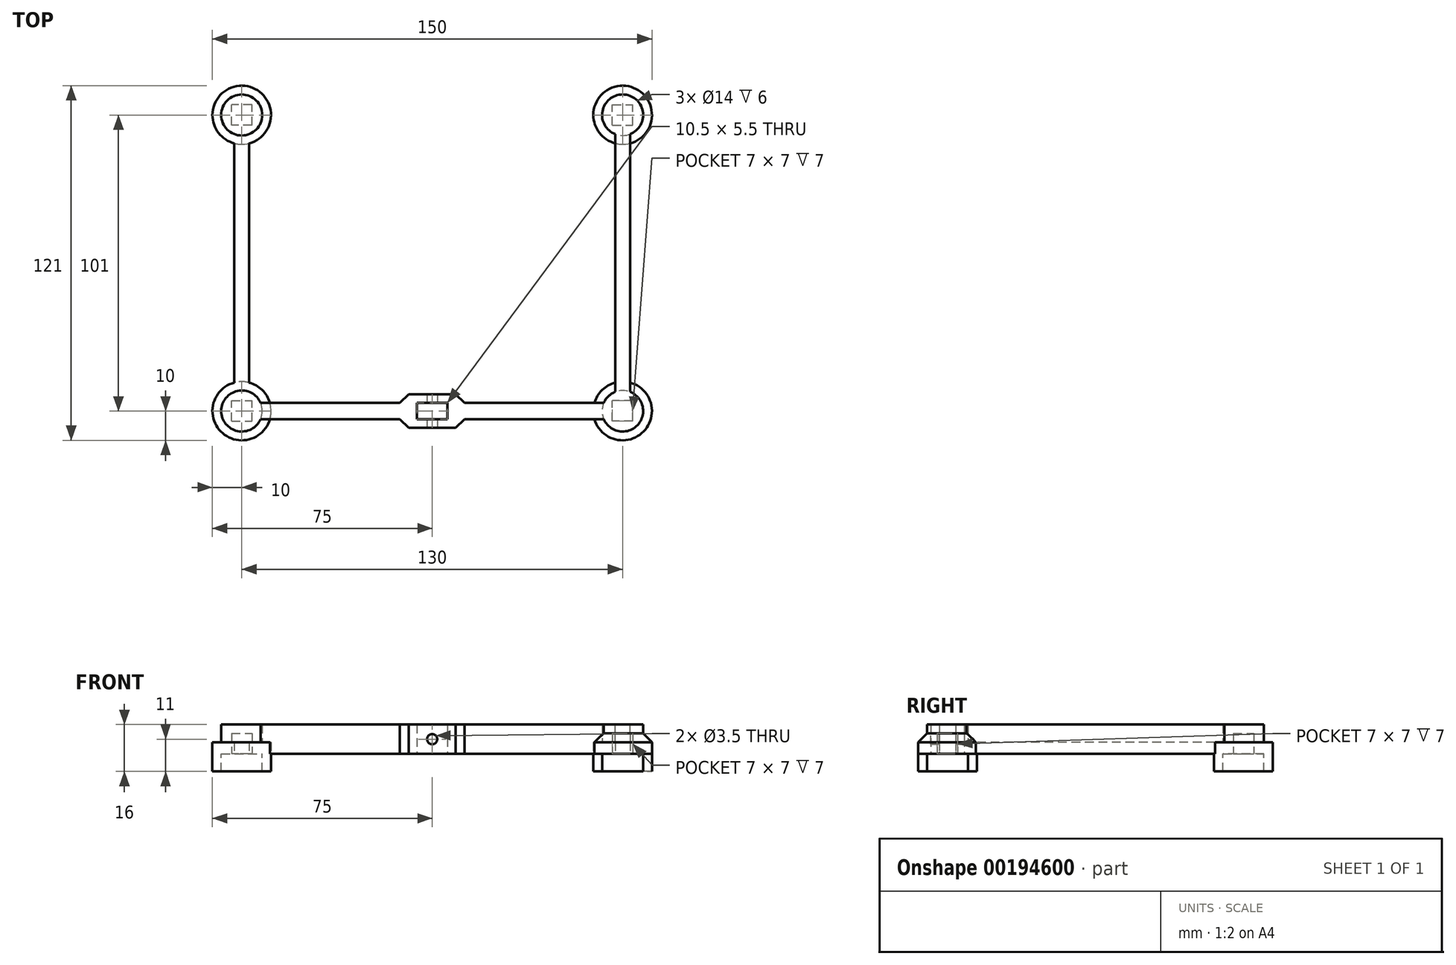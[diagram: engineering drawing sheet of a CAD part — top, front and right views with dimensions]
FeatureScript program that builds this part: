
annotation { "Feature Type Name" : "Feature", "Feature Type Description" : "" }
export const myFeature = defineFeature(function(context is Context, id is Id, definition is map)
    precondition{}
    {
        {
            var Q0;
            Q0=qCreatedBy(makeId("Top.planeOp"),FACE);
            var sketch = newSketch(context, id + "F0", { "sketchPlane" : qUnion([Q0])});
            skLineSegment(sketch, "E0.bottom", {"start": v(-5.25, 2.75) * mm, "end": v(5.25, 2.75) * mm});
            skLineSegment(sketch, "E0.top", {"start": v(-5.25, -2.75) * mm, "end": v(5.25, -2.75) * mm});
            skLineSegment(sketch, "E0.left", {"start": v(-5.25, 2.75) * mm, "end": v(-5.25, -2.75) * mm});
            skLineSegment(sketch, "E0.right", {"start": v(5.25, 2.75) * mm, "end": v(5.25, -2.75) * mm});
            skPoint(sketch, "E0.middle", {"position": v(0, 0) * mm});
            skLineSegment(sketch, "E1.bottom", {"start": v(-8, 5.75) * mm, "end": v(8, 5.75) * mm});
            skLineSegment(sketch, "E1.top", {"start": v(-8, -5.75) * mm, "end": v(8, -5.75) * mm});
            skLineSegment(sketch, "E1.left", {"start": v(-8, 5.75) * mm, "end": v(-8, -5.75) * mm});
            skLineSegment(sketch, "E1.right", {"start": v(8, 5.75) * mm, "end": v(8, -5.75) * mm});
            skLineSegment(sketch, "E2", {"start": v(0, 0) * mm, "end": v(-65, 0) * mm, "construction": true});
            skCircle(sketch, "E3", {"center": v(-65, 0) * mm, "radius": 7 * mm});
            skCircle(sketch, "E4", {"center": v(-65, 0) * mm, "radius": 10 * mm});
            skLineSegment(sketch, "E5", {"start": v(-8, 2.75) * mm, "end": v(-55.39, 2.75) * mm});
            skLineSegment(sketch, "E6", {"start": v(-8, -2.75) * mm, "end": v(-55.39, -2.75) * mm});
            skLineSegment(sketch, "E7.MirrorCS", {"start": v(8, -2.75) * mm, "end": v(55.39, -2.75) * mm});
            skLineSegment(sketch, "E8.MirrorCS", {"start": v(8, 2.75) * mm, "end": v(55.39, 2.75) * mm});
            skCircle(sketch, "E9.MirrorC", {"center": v(65, 0) * mm, "radius": 7 * mm});
            skCircle(sketch, "E10.MirrorC", {"center": v(65, 0) * mm, "radius": 10 * mm});
            skSolve(sketch);
        }
        {
            var Q0;
            Q0=makeQuery(id+"F0.imprint","IMPRINT",FACE,{"disambiguationData":[TD([[makeQuery(id+"F0.imprint","IMPRINT",EDGE,{"derivedFrom":sQuery(id+"F0.wireOp",EDGE,"E3")}),-1.0]])]});
            var Q1;
            Q1=makeQuery(id+"F0.imprint","IMPRINT",FACE,{"disambiguationData":[TD([[makeQuery(id+"F0.imprint","IMPRINT",EDGE,{"derivedFrom":sQuery(id+"F0.wireOp",EDGE,"E9.MirrorC")}),1.0]])]});
            extrude(context, id + "F1", {"entities" : qUnion([Q0, Q1]), "oppositeDirection" : true, "depth" : 6 * mm});
        }
        {
            var Q0;
            {var subQ0=sQuery(id+"F0.wireOp",EDGE,"E5");Q0=makeQuery(id+"F0.imprint","IMPRINT",FACE,{"disambiguationData":[TD([[makeQuery(id+"F0.imprint","IMPRINT",EDGE,{"derivedFrom":subQ0}),1.0]])]});}
            var Q1;
            {var subQ0=sQuery(id+"F0.wireOp",EDGE,"E7.MirrorCS");Q1=makeQuery(id+"F0.imprint","IMPRINT",FACE,{"disambiguationData":[TD([[makeQuery(id+"F0.imprint","IMPRINT",EDGE,{"derivedFrom":subQ0}),1.0]])]});}
            var Q2;
            Q2=makeQuery(id+"F0.imprint","IMPRINT",FACE,{"disambiguationData":[TD([[makeQuery(id+"F0.imprint","IMPRINT",EDGE,{"derivedFrom":sQuery(id+"F0.wireOp",EDGE,"E9.MirrorC")}),1.0]])]});
            var Q3;
            Q3=makeQuery(id+"F0.imprint","IMPRINT",FACE,{"disambiguationData":[TD([[makeQuery(id+"F0.imprint","IMPRINT",EDGE,{"derivedFrom":sQuery(id+"F0.wireOp",EDGE,"E0.bottom")}),1.0]])]});
            var Q4;
            Q4=makeQuery(id+"F0.imprint","IMPRINT",FACE,{"disambiguationData":[TD([[makeQuery(id+"F0.imprint","IMPRINT",EDGE,{"derivedFrom":sQuery(id+"F0.wireOp",EDGE,"E3")}),1.0]])]});
            var Q5;
            Q5=makeQuery(id+"F0.imprint","IMPRINT",FACE,{"disambiguationData":[TD([[makeQuery(id+"F0.imprint","IMPRINT",EDGE,{"derivedFrom":sQuery(id+"F0.wireOp",EDGE,"E3")}),-1.0]])]});
            var Q6;
            Q6=makeQuery(id+"F0.imprint","IMPRINT",FACE,{"disambiguationData":[TD([[makeQuery(id+"F0.imprint","IMPRINT",EDGE,{"derivedFrom":sQuery(id+"F0.wireOp",EDGE,"E9.MirrorC")}),-1.0]])]});
            extrude(context, id + "F2", {"entities" : qUnion([Q0, Q1, Q2, Q3, Q4, Q5, Q6]), "depth" : 4 * mm});
        }
        {
            var Q0;
            Q0=makeQuery(id+"F2.opExtrude","CAP_FACE",FACE,{"disambiguationData":[OSD([sQuery(id+"F0.wireOp",EDGE,"E0.bottom"),sQuery(id+"F0.wireOp",EDGE,"E0.top"),sQuery(id+"F0.wireOp",EDGE,"E0.left"),sQuery(id+"F0.wireOp",EDGE,"E0.right"),sQuery(id+"F0.wireOp",EDGE,"E1.bottom"),sQuery(id+"F0.wireOp",EDGE,"E1.top"),sQuery(id+"F0.wireOp",EDGE,"E1.left"),sQuery(id+"F0.wireOp",EDGE,"E1.right"),sQuery(id+"F0.wireOp",EDGE,"E4"),sQuery(id+"F0.wireOp",EDGE,"E5"),sQuery(id+"F0.wireOp",EDGE,"E6"),sQuery(id+"F0.wireOp",EDGE,"E7.MirrorCS"),sQuery(id+"F0.wireOp",EDGE,"E8.MirrorCS"),sQuery(id+"F0.wireOp",EDGE,"E10.MirrorC")])],"isStart":false});
            var sketch = newSketch(context, id + "F3", { "sketchPlane" : qUnion([Q0])});
            skCircle(sketch, "E11", {"center": v(-65, 0) * mm, "radius": 7 * mm});
            skCircle(sketch, "E12", {"center": v(65, 0) * mm, "radius": 7 * mm});
            skLineSegment(sketch, "E13", {"start": v(-8, 2.75) * mm, "end": v(-58.56, 2.75) * mm});
            skLineSegment(sketch, "E14", {"start": v(-8, -2.75) * mm, "end": v(-58.56, -2.75) * mm});
            skLineSegment(sketch, "E15.bottom", {"start": v(-8, 5.75) * mm, "end": v(8, 5.75) * mm});
            skLineSegment(sketch, "E15.top", {"start": v(-8, -5.75) * mm, "end": v(8, -5.75) * mm});
            skLineSegment(sketch, "E15.left", {"start": v(-8, 5.75) * mm, "end": v(-8, -5.75) * mm});
            skLineSegment(sketch, "E15.right", {"start": v(8, 5.75) * mm, "end": v(8, -5.75) * mm});
            skLineSegment(sketch, "E16.bottom", {"start": v(-5.25, 2.75) * mm, "end": v(5.25, 2.75) * mm});
            skLineSegment(sketch, "E16.top", {"start": v(-5.25, -2.75) * mm, "end": v(5.25, -2.75) * mm});
            skLineSegment(sketch, "E16.left", {"start": v(-5.25, 2.75) * mm, "end": v(-5.25, -2.75) * mm});
            skLineSegment(sketch, "E16.right", {"start": v(5.25, 2.75) * mm, "end": v(5.25, -2.75) * mm});
            skLineSegment(sketch, "E17", {"start": v(8, 2.75) * mm, "end": v(58.56, 2.75) * mm});
            skLineSegment(sketch, "E18", {"start": v(8, -2.75) * mm, "end": v(58.56, -2.75) * mm});
            skSolve(sketch);
        }
        {
            var Q0;
            Q0 = qSketchRegion(id + "F3", true);
            extrude(context, id + "F4", {"entities" : qUnion([Q0]), "operationType" : NewBodyOperationType.ADD, "depth" : 6 * mm});
        }
        {
            var Q0;
            Q0=makeQuery(id+"F2.opExtrude","SWEPT_BODY",BODY,{"disambiguationData":[OSD([sQuery(id+"F0.wireOp",EDGE,"E0.bottom"),sQuery(id+"F0.wireOp",EDGE,"E0.top"),sQuery(id+"F0.wireOp",EDGE,"E0.left"),sQuery(id+"F0.wireOp",EDGE,"E0.right"),sQuery(id+"F0.wireOp",EDGE,"E1.bottom"),sQuery(id+"F0.wireOp",EDGE,"E1.top"),sQuery(id+"F0.wireOp",EDGE,"E1.left"),sQuery(id+"F0.wireOp",EDGE,"E1.right"),sQuery(id+"F0.wireOp",EDGE,"E4"),sQuery(id+"F0.wireOp",EDGE,"E5"),sQuery(id+"F0.wireOp",EDGE,"E6"),sQuery(id+"F0.wireOp",EDGE,"E7.MirrorCS"),sQuery(id+"F0.wireOp",EDGE,"E8.MirrorCS"),sQuery(id+"F0.wireOp",EDGE,"E10.MirrorC")])]});
            var Q1;
            Q1=makeQuery(id+"F1.opExtrude","SWEPT_BODY",BODY,{"disambiguationData":[OSD([sQuery(id+"F0.wireOp",EDGE,"E3"),sQuery(id+"F0.wireOp",EDGE,"E4")])]});
            var Q2;
            Q2=makeQuery(id+"F1.opExtrude","SWEPT_BODY",BODY,{"disambiguationData":[OSD([sQuery(id+"F0.wireOp",EDGE,"E9.MirrorC"),sQuery(id+"F0.wireOp",EDGE,"E10.MirrorC")])]});
            booleanBodies(context, id + "F5", {"operationType" : BooleanOperationType.UNION, "tools" : qUnion([Q0, Q1, Q2])});
        }
        {
            var Q0;
            Q0=makeQuery(id+"F0.imprint","IMPRINT",FACE,{"disambiguationData":[TD([[makeQuery(id+"F0.imprint","IMPRINT",EDGE,{"derivedFrom":sQuery(id+"F0.wireOp",EDGE,"E3")}),1.0]])]});
            var sketch = newSketch(context, id + "F6", { "sketchPlane" : qUnion([Q0])});
            skLineSegment(sketch, "E19", {"start": v(0, 0) * mm, "end": v(-65, 0) * mm, "construction": true});
            skCircle(sketch, "E20", {"center": v(-65, 0) * mm, "radius": 7 * mm});
            skLineSegment(sketch, "E21.bottom", {"start": v(-68.5, -3.5) * mm, "end": v(-61.5, -3.5) * mm});
            skLineSegment(sketch, "E21.top", {"start": v(-68.5, 3.5) * mm, "end": v(-61.5, 3.5) * mm});
            skLineSegment(sketch, "E21.left", {"start": v(-68.5, -3.5) * mm, "end": v(-68.5, 3.5) * mm});
            skLineSegment(sketch, "E21.right", {"start": v(-61.5, -3.5) * mm, "end": v(-61.5, 3.5) * mm});
            skPoint(sketch, "E22.MirrorP", {"position": v(65, 0) * mm});
            skLineSegment(sketch, "E23.MirrorCS", {"start": v(61.5, -3.5) * mm, "end": v(61.5, 3.5) * mm});
            skLineSegment(sketch, "E24.MirrorCS", {"start": v(68.5, -3.5) * mm, "end": v(68.5, 3.5) * mm});
            skLineSegment(sketch, "E25.MirrorCS", {"start": v(68.5, -3.5) * mm, "end": v(61.5, -3.5) * mm});
            skLineSegment(sketch, "E26.MirrorCS", {"start": v(68.5, 3.5) * mm, "end": v(61.5, 3.5) * mm});
            skSolve(sketch);
        }
        {
            var Q0;
            Q0=makeQuery(id+"F6.imprint","IMPRINT",FACE,{"disambiguationData":[TD([[makeQuery(id+"F6.imprint","IMPRINT",EDGE,{"derivedFrom":sQuery(id+"F6.wireOp",EDGE,"E23.MirrorCS")}),-1.0]])]});
            var Q1;
            Q1=makeQuery(id+"F6.imprint","IMPRINT",FACE,{"disambiguationData":[TD([[makeQuery(id+"F6.imprint","IMPRINT",EDGE,{"derivedFrom":sQuery(id+"F6.wireOp",EDGE,"E21.bottom")}),1.0]])]});
            extrude(context, id + "F7", {"entities" : qUnion([Q0, Q1]), "operationType" : NewBodyOperationType.REMOVE, "depth" : 7 * mm});
        }
        {
            var Q0;
            Q0=makeQuery(id+"F4.boolean.opBoolean","MERGE",FACE,{"derivedFrom":[makeQuery(id+"F2.opExtrude","SWEPT_FACE",FACE,{"disambiguationData":[OSD([sQuery(id+"F0.wireOp",EDGE,"E1.top")])]}),makeQuery(id+"F4.opExtrude","SWEPT_FACE",FACE,{"disambiguationData":[OSD([sQuery(id+"F3.wireOp",EDGE,"E15.top")])]})]});
            var sketch = newSketch(context, id + "F8", { "sketchPlane" : qUnion([Q0])});
            skLineSegment(sketch, "E27.bottom", {"start": v(-8, 10) * mm, "end": v(8, 10) * mm, "construction": true});
            skLineSegment(sketch, "E27.top", {"start": v(-8, 0) * mm, "end": v(8, 0) * mm, "construction": true});
            skLineSegment(sketch, "E27.left", {"start": v(-8, 10) * mm, "end": v(-8, 0) * mm, "construction": true});
            skLineSegment(sketch, "E27.right", {"start": v(8, 10) * mm, "end": v(8, 0) * mm, "construction": true});
            skLineSegment(sketch, "E28", {"start": v(8, 10) * mm, "end": v(-8, 0) * mm, "construction": true});
            skLineSegment(sketch, "E29", {"start": v(-8, 10) * mm, "end": v(8, 0) * mm, "construction": true});
            skPoint(sketch, "E30", {"position": v(0, 5) * mm});
            skCircle(sketch, "E31", {"center": v(0, 5) * mm, "radius": 1.75 * mm});
            skSolve(sketch);
        }
        {
            var Q0;
            Q0=makeQuery(id+"F8.imprint","IMPRINT",FACE,{"disambiguationData":[TD([[makeQuery(id+"F8.imprint","IMPRINT",EDGE,{"derivedFrom":sQuery(id+"F8.wireOp",EDGE,"E31")}),1.0]])]});
            extrude(context, id + "F9", {"entities" : qUnion([Q0]), "operationType" : NewBodyOperationType.REMOVE, "endBound" : BoundingType.THROUGH_ALL, "oppositeDirection" : true, "depth" : 25 * mm});
        }
        {
            var Q0;
            {var subQ0=sQuery(id+"F0.wireOp",EDGE,"E6");var subQ1=sQuery(id+"F0.wireOp",EDGE,"E5");var subQ2=sQuery(id+"F0.wireOp",EDGE,"E4");var subQ3=sQuery(id+"F0.wireOp",EDGE,"E1.right");var subQ4=sQuery(id+"F0.wireOp",EDGE,"E1.top");var subQ5=sQuery(id+"F0.wireOp",EDGE,"E7.MirrorCS");var subQ9=sQuery(id+"F0.wireOp",EDGE,"E1.bottom");var subQ10=sQuery(id+"F0.wireOp",EDGE,"E8.MirrorCS");var subQ14=sQuery(id+"F0.wireOp",EDGE,"E0.bottom");var subQ15=sQuery(id+"F0.wireOp",EDGE,"E0.top");var subQ16=sQuery(id+"F0.wireOp",EDGE,"E10.MirrorC");var subQ17=sQuery(id+"F0.wireOp",EDGE,"E0.left");var subQ19=sQuery(id+"F0.wireOp",EDGE,"E1.left");var subQ20=sQuery(id+"F0.wireOp",EDGE,"E0.right");Q0=makeQuery(id+"F5.opBoolean","SPLIT",FACE,{"disambiguationData":[TD([makeQuery(id+"F1.opExtrude","SWEPT_FACE",FACE,{"disambiguationData":[OSD([subQ2])]})])],"derivedFrom":makeQuery(id+"F2.opExtrude","CAP_FACE",FACE,{"disambiguationData":[OSD([subQ14,subQ15,subQ17,subQ20,subQ9,subQ4,subQ19,subQ3,subQ2,subQ1,subQ0,subQ5,subQ10,subQ16])],"isStart":true})});}
            var sketch = newSketch(context, id + "F10", { "sketchPlane" : qUnion([Q0])});
            skLineSegment(sketch, "E32", {"start": v(0, 0) * mm, "end": v(-65, 0) * mm, "construction": true});
            skLineSegment(sketch, "E33", {"start": v(0, 0) * mm, "end": v(65, 0) * mm, "construction": true});
            skLineSegment(sketch, "E34", {"start": v(-65, 0) * mm, "end": v(-65, -101) * mm, "construction": true});
            skArc(sketch, "E35", {"start": v(-67.5, -91.32) * mm, "mid": v(-65, -111) * mm, "end": v(-62.5, -91.32) * mm});
            skLineSegment(sketch, "E36.left", {"start": v(-67.5, -91.32) * mm, "end": v(-67.5, -9.68) * mm});
            skLineSegment(sketch, "E36.right", {"start": v(-62.5, -91.32) * mm, "end": v(-62.5, -9.68) * mm});
            skPoint(sketch, "E36.middle", {"position": v(-65, -50.5) * mm});
            skArc(sketch, "E37", {"start": v(-67.5, -9.68) * mm, "mid": v(-65, -10) * mm, "end": v(-62.5, -9.68) * mm});
            skLineSegment(sketch, "E38.MirrorCS", {"start": v(67.5, -91.32) * mm, "end": v(67.5, -9.68) * mm});
            skArc(sketch, "E39.MirrorCS", {"start": v(67.5, -91.32) * mm, "mid": v(65, -111) * mm, "end": v(62.5, -91.32) * mm});
            skArc(sketch, "E40.MirrorCS", {"start": v(67.5, -9.68) * mm, "mid": v(65, -10) * mm, "end": v(62.5, -9.68) * mm});
            skPoint(sketch, "E41.MirrorP", {"position": v(65, -50.5) * mm});
            skLineSegment(sketch, "E42", {"start": v(62.5, -91.32) * mm, "end": v(62.5, -9.68) * mm});
            skSolve(sketch);
        }
        {
            var Q0;
            Q0 = qSketchRegion(id + "F10", true);
            extrude(context, id + "F11", {"entities" : qUnion([Q0]), "operationType" : NewBodyOperationType.ADD, "oppositeDirection" : true, "depth" : 4 * mm});
        }
        {
            var Q0;
            Q0=makeQuery(id+"F11.opExtrude","CAP_FACE",FACE,{"disambiguationData":[OSD([sQuery(id+"F10.wireOp",EDGE,"E35"),sQuery(id+"F10.wireOp",EDGE,"E36.left"),sQuery(id+"F10.wireOp",EDGE,"E36.right"),sQuery(id+"F10.wireOp",EDGE,"E37")])],"isStart":true});
            var sketch = newSketch(context, id + "F12", { "sketchPlane" : qUnion([Q0])});
            skCircle(sketch, "E43", {"center": v(-65, -101) * mm, "radius": 10 * mm});
            skCircle(sketch, "E44", {"center": v(-65, -101) * mm, "radius": 7 * mm});
            skCircle(sketch, "E45.MirrorC", {"center": v(65, -101) * mm, "radius": 10 * mm});
            skCircle(sketch, "E46.MirrorC", {"center": v(65, -101) * mm, "radius": 7 * mm});
            skSolve(sketch);
        }
        {
            var Q0;
            Q0 = qSketchRegion(id + "F12", true);
            extrude(context, id + "F13", {"entities" : qUnion([Q0]), "operationType" : NewBodyOperationType.ADD, "depth" : 6 * mm});
        }
        {
            var Q0;
            Q0=makeQuery(id+"F11.opExtrude","CAP_FACE",FACE,{"disambiguationData":[OSD([sQuery(id+"F10.wireOp",EDGE,"E35"),sQuery(id+"F10.wireOp",EDGE,"E36.left"),sQuery(id+"F10.wireOp",EDGE,"E36.right"),sQuery(id+"F10.wireOp",EDGE,"E37")])],"isStart":false});
            var sketch = newSketch(context, id + "F14", { "sketchPlane" : qUnion([Q0])});
            skCircle(sketch, "E47", {"center": v(-65, 101) * mm, "radius": 7 * mm});
            skCircle(sketch, "E48.MirrorC", {"center": v(65, 101) * mm, "radius": 7 * mm});
            skSolve(sketch);
        }
        {
            var Q0;
            Q0 = qSketchRegion(id + "F14", true);
            extrude(context, id + "F15", {"entities" : qUnion([Q0]), "operationType" : NewBodyOperationType.ADD, "depth" : 6 * mm});
        }
        {
            var Q0;
            Q0=makeQuery(id+"F15.opExtrude","CAP_FACE",FACE,{"disambiguationData":[OSD([sQuery(id+"F14.wireOp",EDGE,"E48.MirrorC")])],"isStart":false});
            var sketch = newSketch(context, id + "F16", { "sketchPlane" : qUnion([Q0])});
            skCircle(sketch, "E49", {"center": v(65, 101) * mm, "radius": 7 * mm, "construction": true});
            skCircle(sketch, "E50", {"center": v(65, 0) * mm, "radius": 7 * mm, "construction": true});
            skLineSegment(sketch, "E51", {"start": v(62.5, 6.54) * mm, "end": v(62.5, 94.46) * mm});
            skLineSegment(sketch, "E52", {"start": v(67.5, 6.54) * mm, "end": v(67.5, 94.46) * mm});
            skArc(sketch, "E53", {"start": v(62.5, 94.46) * mm, "mid": v(65, 94) * mm, "end": v(67.5, 94.46) * mm});
            skArc(sketch, "E54", {"start": v(62.5, 6.54) * mm, "mid": v(65, 7) * mm, "end": v(67.5, 6.54) * mm});
            skSolve(sketch);
        }
        {
            var Q0;
            Q0 = qSketchRegion(id + "F16", true);
            extrude(context, id + "F17", {"entities" : qUnion([Q0]), "operationType" : NewBodyOperationType.ADD, "endBound" : BoundingType.UP_TO_NEXT, "oppositeDirection" : true, "depth" : 25 * mm});
        }
        {
            var Q0;
            {var subQ0=sQuery(id+"F3.wireOp",EDGE,"E12");var subQ1=sQuery(id+"F0.wireOp",EDGE,"E8.MirrorCS");Q0=makeQuery(id+"F17.boolean.opBoolean","SPLIT",EDGE,{"disambiguationData":[TD([makeQuery(id+"F2.opExtrude","SWEPT_FACE",FACE,{"disambiguationData":[OSD([subQ1])]})])],"derivedFrom":makeQuery(id+"F4.opExtrude","CAP_EDGE",EDGE,{"disambiguationData":[OSD([subQ0])],"isStart":true})});}
            var Q1;
            Q1=makeQuery(id+"F15.opExtrude","CAP_EDGE",EDGE,{"disambiguationData":[OSD([sQuery(id+"F14.wireOp",EDGE,"E48.MirrorC")])],"isStart":true});
            var Q2;
            Q2=makeQuery(id+"F15.opExtrude","CAP_EDGE",EDGE,{"disambiguationData":[OSD([sQuery(id+"F14.wireOp",EDGE,"E47")])],"isStart":true});
            var Q3;
            {var subQ0=sQuery(id+"F3.wireOp",EDGE,"E11");var subQ1=sQuery(id+"F0.wireOp",EDGE,"E6");Q3=makeQuery(id+"F17.boolean.opBoolean","SPLIT",EDGE,{"disambiguationData":[TD([makeQuery(id+"F2.opExtrude","SWEPT_FACE",FACE,{"disambiguationData":[OSD([subQ1])]})])],"derivedFrom":makeQuery(id+"F4.opExtrude","CAP_EDGE",EDGE,{"disambiguationData":[OSD([subQ0])],"isStart":true})});}
            var Q4;
            {var subQ0=sQuery(id+"F3.wireOp",EDGE,"E11");var subQ1=sQuery(id+"F0.wireOp",EDGE,"E5");Q4=makeQuery(id+"F17.boolean.opBoolean","SPLIT",EDGE,{"disambiguationData":[TD([makeQuery(id+"F2.opExtrude","SWEPT_FACE",FACE,{"disambiguationData":[OSD([subQ1])]})])],"derivedFrom":makeQuery(id+"F4.opExtrude","CAP_EDGE",EDGE,{"disambiguationData":[OSD([subQ0])],"isStart":true})});}
            var Q5;
            {var subQ0=sQuery(id+"F3.wireOp",EDGE,"E12");var subQ1=sQuery(id+"F0.wireOp",EDGE,"E7.MirrorCS");Q5=makeQuery(id+"F17.boolean.opBoolean","SPLIT",EDGE,{"disambiguationData":[TD([makeQuery(id+"F2.opExtrude","SWEPT_FACE",FACE,{"disambiguationData":[OSD([subQ1])]})])],"derivedFrom":makeQuery(id+"F4.opExtrude","CAP_EDGE",EDGE,{"disambiguationData":[OSD([subQ0])],"isStart":true})});}
            chamfer(context, id + "F18", {"entities" : qUnion([Q0, Q1, Q2, Q3, Q4, Q5]), "width" : 3 * mm, "tangentPropagation" : true});
        }
        {
            var Q0;
            Q0=makeQuery(id+"F13.boolean.opBoolean","SPLIT",FACE,{"disambiguationData":[TD([makeQuery(id+"F13.opExtrude","SWEPT_FACE",FACE,{"disambiguationData":[OSD([sQuery(id+"F12.wireOp",EDGE,"E44")])]})])],"derivedFrom":makeQuery(id+"F11.opExtrude","CAP_FACE",FACE,{"disambiguationData":[OSD([sQuery(id+"F10.wireOp",EDGE,"E35"),sQuery(id+"F10.wireOp",EDGE,"E36.left"),sQuery(id+"F10.wireOp",EDGE,"E36.right"),sQuery(id+"F10.wireOp",EDGE,"E37")])],"isStart":true})});
            var sketch = newSketch(context, id + "F19", { "sketchPlane" : qUnion([Q0])});
            skLineSegment(sketch, "E55.bottom", {"start": v(-61.5, -97.5) * mm, "end": v(-68.5, -97.5) * mm});
            skLineSegment(sketch, "E55.top", {"start": v(-61.5, -104.5) * mm, "end": v(-68.5, -104.5) * mm});
            skLineSegment(sketch, "E55.left", {"start": v(-61.5, -97.5) * mm, "end": v(-61.5, -104.5) * mm});
            skLineSegment(sketch, "E55.right", {"start": v(-68.5, -97.5) * mm, "end": v(-68.5, -104.5) * mm});
            skPoint(sketch, "E55.middle", {"position": v(-65, -101) * mm});
            skLineSegment(sketch, "E56.MirrorCS", {"start": v(68.5, -97.5) * mm, "end": v(68.5, -104.5) * mm});
            skLineSegment(sketch, "E57.MirrorCS", {"start": v(61.5, -97.5) * mm, "end": v(61.5, -104.5) * mm});
            skLineSegment(sketch, "E58.MirrorCS", {"start": v(61.5, -97.5) * mm, "end": v(68.5, -97.5) * mm});
            skLineSegment(sketch, "E59.MirrorCS", {"start": v(61.5, -104.5) * mm, "end": v(68.5, -104.5) * mm});
            skPoint(sketch, "E60.MirrorP", {"position": v(65, -101) * mm});
            skSolve(sketch);
        }
        {
            var Q0;
            Q0 = qSketchRegion(id + "F19", true);
            extrude(context, id + "F20", {"entities" : qUnion([Q0]), "operationType" : NewBodyOperationType.REMOVE, "oppositeDirection" : true, "depth" : 7 * mm});
        }
        {
            var Q0;
            Q0=makeQuery(id+"F4.boolean.opBoolean","MERGE",EDGE,{"derivedFrom":[makeQuery(id+"F2.opExtrude","SWEPT_EDGE",EDGE,{"disambiguationData":[OSD([sQuery(id+"F0.wireOp",EDGE,"E1.right"),sQuery(id+"F0.wireOp",EDGE,"E7.MirrorCS")])]}),makeQuery(id+"F4.opExtrude","SWEPT_EDGE",EDGE,{"disambiguationData":[OSD([sQuery(id+"F3.wireOp",EDGE,"E15.right"),sQuery(id+"F3.wireOp",EDGE,"E18")])]})]});
            var Q1;
            Q1=makeQuery(id+"F4.boolean.opBoolean","MERGE",EDGE,{"derivedFrom":[makeQuery(id+"F2.opExtrude","SWEPT_EDGE",EDGE,{"disambiguationData":[OSD([sQuery(id+"F0.wireOp",EDGE,"E1.left"),sQuery(id+"F0.wireOp",EDGE,"E6")])]}),makeQuery(id+"F4.opExtrude","SWEPT_EDGE",EDGE,{"disambiguationData":[OSD([sQuery(id+"F3.wireOp",EDGE,"E14"),sQuery(id+"F3.wireOp",EDGE,"E15.left")])]})]});
            var Q2;
            Q2=makeQuery(id+"F4.boolean.opBoolean","MERGE",EDGE,{"derivedFrom":[makeQuery(id+"F2.opExtrude","SWEPT_EDGE",EDGE,{"disambiguationData":[OSD([sQuery(id+"F0.wireOp",EDGE,"E1.right"),sQuery(id+"F0.wireOp",EDGE,"E8.MirrorCS")])]}),makeQuery(id+"F4.opExtrude","SWEPT_EDGE",EDGE,{"disambiguationData":[OSD([sQuery(id+"F3.wireOp",EDGE,"E15.right"),sQuery(id+"F3.wireOp",EDGE,"E17")])]})]});
            var Q3;
            Q3=makeQuery(id+"F4.boolean.opBoolean","MERGE",EDGE,{"derivedFrom":[makeQuery(id+"F2.opExtrude","SWEPT_EDGE",EDGE,{"disambiguationData":[OSD([sQuery(id+"F0.wireOp",EDGE,"E1.left"),sQuery(id+"F0.wireOp",EDGE,"E5")])]}),makeQuery(id+"F4.opExtrude","SWEPT_EDGE",EDGE,{"disambiguationData":[OSD([sQuery(id+"F3.wireOp",EDGE,"E13"),sQuery(id+"F3.wireOp",EDGE,"E15.left")])]})]});
            chamfer(context, id + "F21", {"entities" : qUnion([Q0, Q1, Q2, Q3]), "width" : 3 * mm, "tangentPropagation" : true});
        }
    });
